# Revit family: revitupgrade
name_source: partatom
category: Furniture
units: mm (PartAtom-declared; Revit-internal decimal feet)

## family parameters
Always vertical = Yes
Cut with Voids When Loaded = No
Enable Cutting in Views = No
OmniClass Number = 23.40.70.14.64.11
OmniClass Title = Office Furniture
Render Appearance Source = Family Geometry
Room Calculation Point = No
Shared = No
Work Plane-Based = No

## types (6) — shared parameters
Assembly Code = E2020200
Casters = Yes
Default Elevation = 0.00"
Depth = 36.00"
Description = Planner® desks and tables deliver via a heavy-duty, steel frame and leg system. This line is suited to a variety of subjects, including art, maker labs, STEM learning, and more.
Leg Adjust = 4.73"
Manufacturer = Smith System
Release Date = February 2024
URL = https://www.steelcase.com

## per-type parameters (varying)
| type | A | Height | Leg Dist | Style Number(s) | Width |
| 36D x 60W x 40H | 13.50" | 40.00" | 38.87" | SMPLN25210, SMPLN25210L | 60.00" |
| 36D x 72W x 40H | 13.50" | 40.00" | 38.87" | SMPLN25216, SMPLN25216L | 72.00" |
| 36D x 60W x 36H | 13.50" | 36.00" | 34.87" | SMPLN25208, SMPLN25208L | 60.00" |
| 36D x 72W x 36H | 13.50" | 36.00" | 34.87" | SMPLN25214, SMPLN25214L | 72.00" |
| 36D x 60W x 29H | 18.00" | 29.00" | 27.87" | SMPLN25206, SMPLN25206L | 60.00" |
| 36D x 72W x 29H | 18.00" | 29.00" | 27.87" | SMPLN25212, SMPLN25212L | 72.00" |

## geometry (parser evidence)
native form markers: Sweep x4
no freeform markers — native parametric forms only
